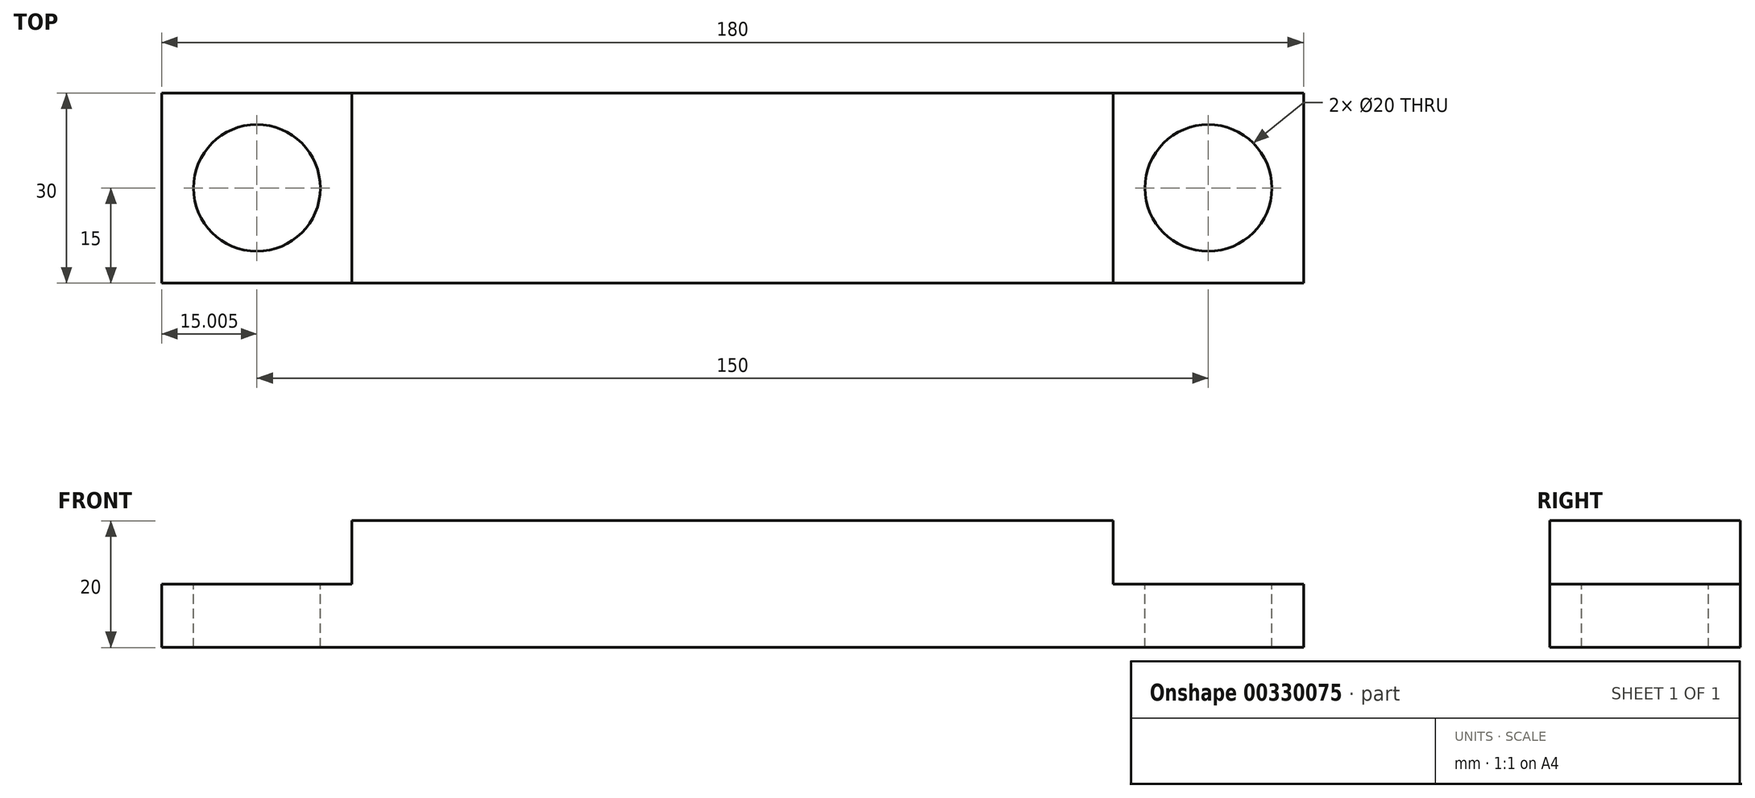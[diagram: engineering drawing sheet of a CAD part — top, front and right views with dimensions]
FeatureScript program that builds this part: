
annotation { "Feature Type Name" : "Feature", "Feature Type Description" : "" }
export const myFeature = defineFeature(function(context is Context, id is Id, definition is map)
    precondition{}
    {
        {
            var Q0;
            Q0=qCreatedBy(makeId("Front.planeOp"),FACE);
            var sketch = newSketch(context, id + "F0", { "sketchPlane" : qUnion([Q0])});
            skLineSegment(sketch, "E0", {"start": v(-91.38, 28.37) * mm, "end": v(88.62, 28.37) * mm});
            skLineSegment(sketch, "E1", {"start": v(88.62, 28.37) * mm, "end": v(88.62, 38.37) * mm});
            skLineSegment(sketch, "E2", {"start": v(58.62, 48.37) * mm, "end": v(-61.38, 48.37) * mm});
            skLineSegment(sketch, "E3", {"start": v(-91.38, 38.37) * mm, "end": v(-91.38, 28.37) * mm});
            skLineSegment(sketch, "E4", {"start": v(-91.38, 38.37) * mm, "end": v(-61.38, 38.37) * mm});
            skLineSegment(sketch, "E5", {"start": v(-61.38, 38.37) * mm, "end": v(-61.38, 48.37) * mm});
            skLineSegment(sketch, "E6", {"start": v(88.62, 38.37) * mm, "end": v(58.62, 38.37) * mm});
            skLineSegment(sketch, "E7", {"start": v(58.62, 38.37) * mm, "end": v(58.62, 48.37) * mm});
            skSolve(sketch);
        }
        {
            var Q0;
            Q0 = qSketchRegion(id + "F0", true);
            extrude(context, id + "F1", {"entities" : qUnion([Q0]), "depth" : 30 * mm, "offsetDistance" : 25 * mm});
        }
        {
            var Q0;
            Q0=makeQuery(id+"F1.opExtrude","SWEPT_FACE",FACE,{"disambiguationData":[OSD([sQuery(id+"F0.wireOp",EDGE,"E6")])]});
            var sketch = newSketch(context, id + "F2", { "sketchPlane" : qUnion([Q0])});
            skLineSegment(sketch, "E8", {"start": v(88.62, -15) * mm, "end": v(83.62, -15) * mm});
            skLineSegment(sketch, "E9", {"start": v(73.62, 0) * mm, "end": v(73.62, -5) * mm});
            skCircle(sketch, "E10", {"center": v(73.62, -15) * mm, "radius": 10 * mm});
            skLineSegment(sketch, "E11.trimOffspring", {"start": v(73.62, -25) * mm, "end": v(73.62, -30) * mm});
            skLineSegment(sketch, "E12.trimOffspring", {"start": v(63.62, -15) * mm, "end": v(58.62, -15) * mm});
            skSolve(sketch);
        }
        {
            var Q0;
            Q0=makeQuery(id+"F1.opExtrude","SWEPT_FACE",FACE,{"disambiguationData":[OSD([sQuery(id+"F0.wireOp",EDGE,"E4")])]});
            var sketch = newSketch(context, id + "F3", { "sketchPlane" : qUnion([Q0])});
            skLineSegment(sketch, "E13", {"start": v(-61.38, -15) * mm, "end": v(-66.38, -15) * mm});
            skLineSegment(sketch, "E14", {"start": v(-76.38, 0) * mm, "end": v(-76.38, -5) * mm});
            skCircle(sketch, "E15", {"center": v(-76.38, -15) * mm, "radius": 10 * mm});
            skLineSegment(sketch, "E16.trimOffspring", {"start": v(-76.38, -25) * mm, "end": v(-76.38, -30) * mm});
            skLineSegment(sketch, "E17.trimOffspring", {"start": v(-86.38, -15) * mm, "end": v(-91.38, -15) * mm});
            skSolve(sketch);
        }
        {
            var Q0;
            {var subQ0=sQuery(id+"F2.wireOp",EDGE,"E10");var subQ1=makeQuery(id+"F2.imprint","INTERSECT",VERTEX,{"derivedFrom":[sQuery(id+"F2.wireOp",EDGE,"E8"),subQ0]});Q0=makeQuery(id+"F2.imprint","IMPRINT",FACE,{"disambiguationData":[TD([[makeQuery(id+"F2.imprint","IMPRINT",EDGE,{"disambiguationData":[TD([[subQ1,-1.0]])],"derivedFrom":subQ0}),1.0]])]});}
            extrude(context, id + "F4", {"entities" : qUnion([Q0]), "operationType" : NewBodyOperationType.REMOVE, "oppositeDirection" : true, "depth" : 25 * mm, "offsetDistance" : 25 * mm});
        }
        {
            var Q0;
            {var subQ0=sQuery(id+"F3.wireOp",EDGE,"E15");var subQ1=makeQuery(id+"F3.imprint","INTERSECT",VERTEX,{"derivedFrom":[sQuery(id+"F3.wireOp",EDGE,"E13"),subQ0]});Q0=makeQuery(id+"F3.imprint","IMPRINT",FACE,{"disambiguationData":[TD([[makeQuery(id+"F3.imprint","IMPRINT",EDGE,{"disambiguationData":[TD([[subQ1,-1.0]])],"derivedFrom":subQ0}),1.0]])]});}
            extrude(context, id + "F5", {"entities" : qUnion([Q0]), "operationType" : NewBodyOperationType.REMOVE, "oppositeDirection" : true, "depth" : 25 * mm, "offsetDistance" : 25 * mm});
        }
    });
